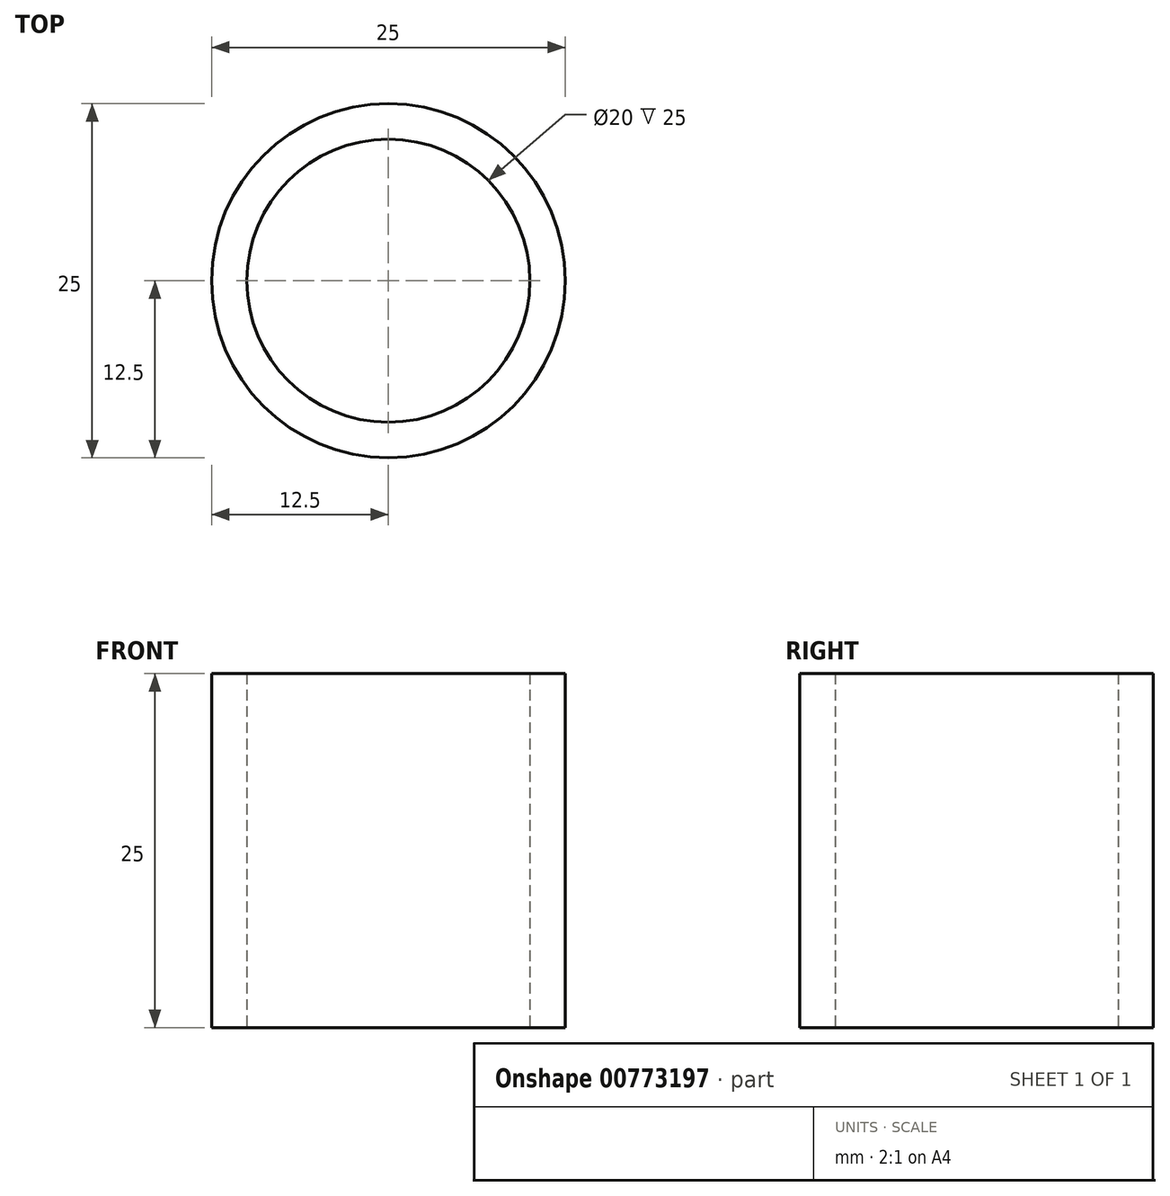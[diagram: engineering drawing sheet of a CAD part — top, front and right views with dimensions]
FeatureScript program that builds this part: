
annotation { "Feature Type Name" : "Feature", "Feature Type Description" : "" }
export const myFeature = defineFeature(function(context is Context, id is Id, definition is map)
    precondition{}
    {
        {
            var Q0;
            Q0=qCreatedBy(makeId("Front.planeOp"),FACE);
            var sketch = newSketch(context, id + "F0", { "sketchPlane" : qUnion([Q0])});
            skLineSegment(sketch, "E0.bottom", {"start": v(13.42, -12.6) * mm, "end": v(-13.42, -12.6) * mm});
            skLineSegment(sketch, "E0.top", {"start": v(13.42, -18.94) * mm, "end": v(-13.42, -18.94) * mm});
            skLineSegment(sketch, "E0.left", {"start": v(13.42, -12.6) * mm, "end": v(13.42, -18.94) * mm});
            skLineSegment(sketch, "E0.right", {"start": v(-13.42, -12.6) * mm, "end": v(-13.42, -18.94) * mm});
            skPoint(sketch, "E0.middle", {"position": v(0, -15.77) * mm});
            skSolve(sketch);
        }
        {
            var Q0;
            Q0=qCreatedBy(makeId("Front.planeOp"),FACE);
            var sketch = newSketch(context, id + "F1", { "sketchPlane" : qUnion([Q0])});
            skFitSpline(sketch, "E1", {"points": [v(-12.43, 4.9) * mm, v(-26.93, 0) * mm, v(-27.48, -27.95) * mm], "startDerivative": vector(-74.18, 2.65) * mm, "endDerivative": vector(1.86, -70.85) * mm});
            skLineSegment(sketch, "E2", {"start": v(-27.48, -27.95) * mm, "end": v(-13.55, -19.2) * mm, "construction": true});
            skLineSegment(sketch, "E3", {"start": v(-13.55, -19.2) * mm, "end": v(-27.77, -19.2) * mm, "construction": true});
            skLineSegment(sketch, "E4", {"start": v(-27.77, -19.2) * mm, "end": v(-27.48, -27.95) * mm});
            skSolve(sketch);
        }
        {
            var Q0;
            Q0=sQuery(id+"F1.wireOp",EDGE,"E1");
            var Q1;
            Q1=sQuery(id+"F1.wireOp",VERTEX,"E1.end");
            cPlane(context, id + "F2", {"entities" : qUnion([Q0, Q1]), "cplaneType" : CPlaneType.CURVE_POINT, "offset" : 25 * mm, "width" : 150 * mm, "height" : 150 * mm});
        }
        {
            var Q0;
            Q0=qCreatedBy(id+"F2.planeOp",FACE);
            var sketch = newSketch(context, id + "F3", { "sketchPlane" : qUnion([Q0])});
            skCircle(sketch, "E5", {"center": v(-28.64, 0) * mm, "radius": 2.25 * mm});
            skCircle(sketch, "E6", {"center": v(-28.64, 0) * mm, "radius": 4.5 * mm});
            skSolve(sketch);
        }
        {
            var Q0;
            Q0=qCreatedBy(makeId("Front.planeOp"),FACE);
            var sketch = newSketch(context, id + "F4", { "sketchPlane" : qUnion([Q0])});
            skLineSegment(sketch, "E7", {"start": v(0, 0) * mm, "end": v(10, 0) * mm, "construction": true});
            skLineSegment(sketch, "E8", {"start": v(10, 0) * mm, "end": v(12.5, 0) * mm, "construction": true});
            skLineSegment(sketch, "E9", {"start": v(0, 0) * mm, "end": v(0, 12.5) * mm, "construction": true});
            skLineSegment(sketch, "E10", {"start": v(0, 0) * mm, "end": v(0, -12.5) * mm, "construction": true});
            skLineSegment(sketch, "E11", {"start": v(10, 12.5) * mm, "end": v(12.5, 12.5) * mm, "construction": true});
            skLineSegment(sketch, "E12", {"start": v(12.5, 12.5) * mm, "end": v(12.5, -12.5) * mm});
            skLineSegment(sketch, "E13", {"start": v(12.5, -12.5) * mm, "end": v(10, -12.5) * mm});
            skLineSegment(sketch, "E14", {"start": v(10, -12.5) * mm, "end": v(10, 12.5) * mm});
            skLineSegment(sketch, "E15", {"start": v(12.5, 12.5) * mm, "end": v(10, 12.5) * mm});
            skSolve(sketch);
        }
        {
            var Q0;
            Q0=makeQuery(id+"F4.imprint","IMPRINT",FACE,{"disambiguationData":[TD([[makeQuery(id+"F4.imprint","IMPRINT",EDGE,{"derivedFrom":sQuery(id+"F4.wireOp",EDGE,"E12")}),-1.0]])]});
            var Q1;
            Q1=sQuery(id+"F4.wireOp",EDGE,"E9");
            revolve(context, id + "F5", {"surfaceOperationType" : NewSurfaceOperationType.NEW, "entities" : qUnion([Q0]), "axis" : qUnion([Q1]), "revolveType" : RevolveType.FULL});
        }
    });
